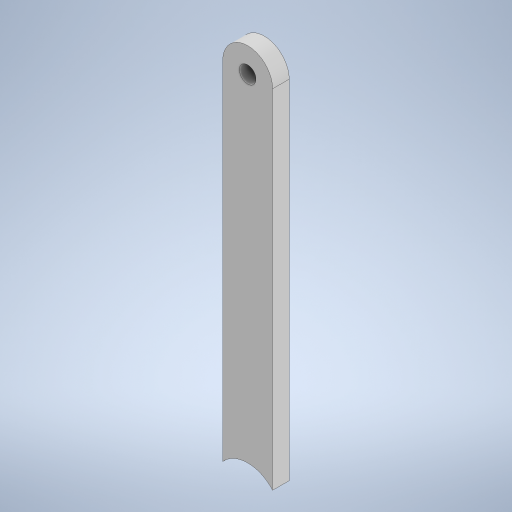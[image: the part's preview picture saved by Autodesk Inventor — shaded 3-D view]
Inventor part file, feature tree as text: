
AUTODESK INVENTOR PART (.ipt)
format: ipt  version: 2023 (Build 270158000, 158)  size: 235,520 bytes
history: native  units: in
note: dims shown in document units (in); Inventor stores cm internally (conversion verified against a paired STEP export)
features: extrude x1, sketch x1
ambient origin geometry x8: Origin, YZ Plane, XZ Plane, XY Plane, X Axis, Y Axis, Z Axis, Center Point
bodies: Solid1 (feature_tree)
feature tree (2):
  extrude  "Extrusion1"  Depth=0.0312in
  sketch  "Sketch1"  dims[d4=0.743in d5=0.125in d6=0.0312in d7=0.0in]
